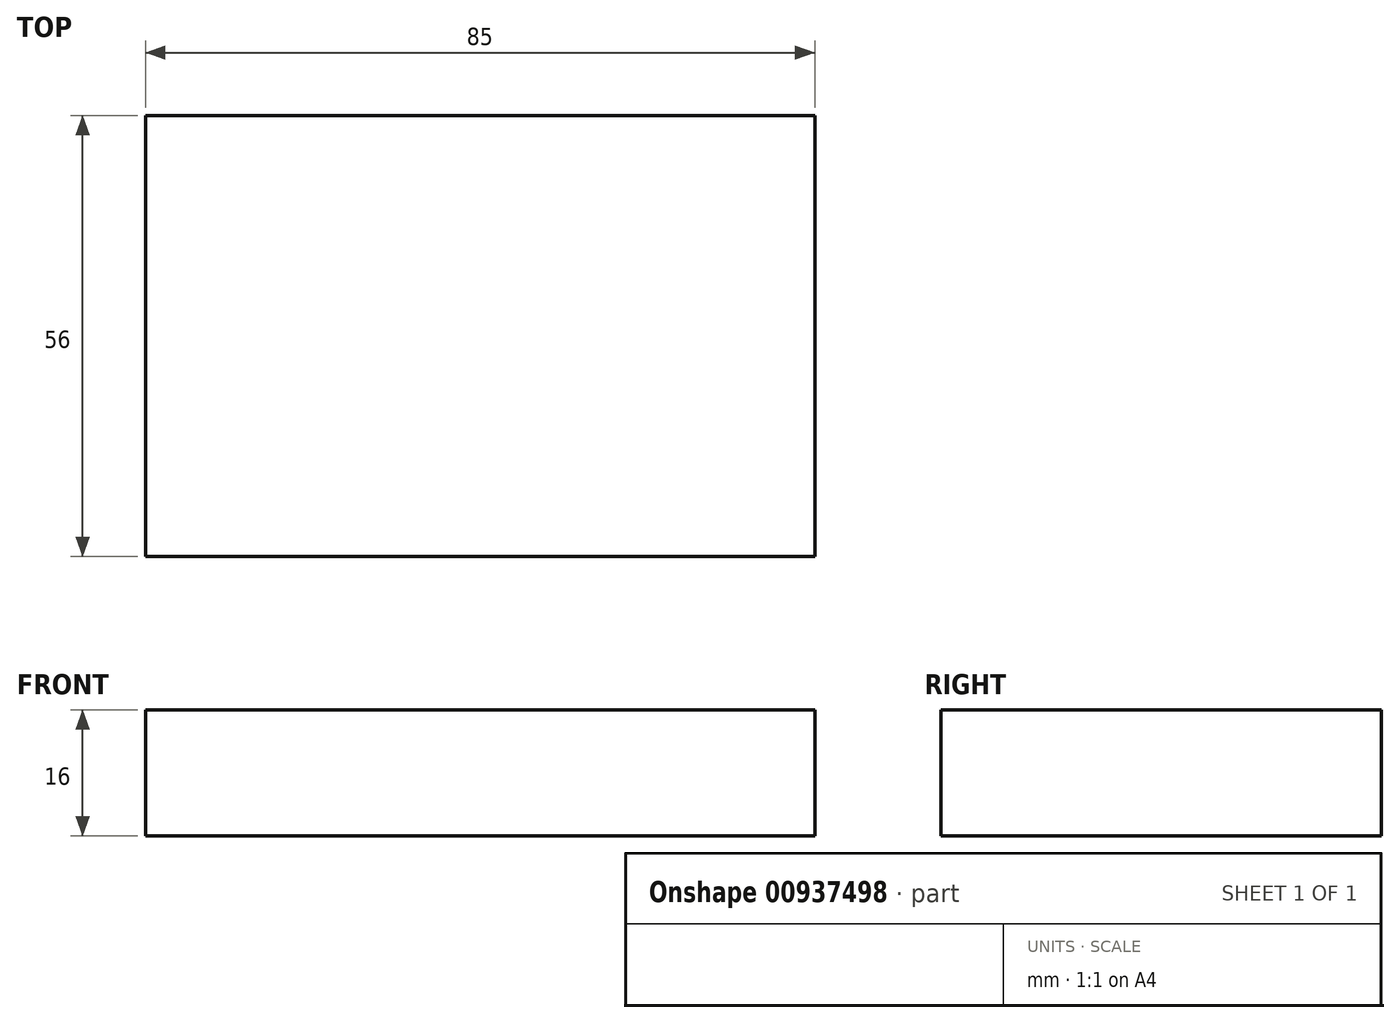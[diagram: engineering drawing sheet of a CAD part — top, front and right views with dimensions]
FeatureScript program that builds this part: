
annotation { "Feature Type Name" : "Feature", "Feature Type Description" : "" }
export const myFeature = defineFeature(function(context is Context, id is Id, definition is map)
    precondition{}
    {
        {
            var Q0;
            Q0=qCreatedBy(makeId("Top.planeOp"),FACE);
            var sketch = newSketch(context, id + "F0", { "sketchPlane" : qUnion([Q0])});
            skLineSegment(sketch, "E0.bottom", {"start": v(42.5, -28) * mm, "end": v(-42.5, -28) * mm});
            skLineSegment(sketch, "E0.top", {"start": v(42.5, 28) * mm, "end": v(-42.5, 28) * mm});
            skLineSegment(sketch, "E0.left", {"start": v(42.5, -28) * mm, "end": v(42.5, 28) * mm});
            skLineSegment(sketch, "E0.right", {"start": v(-42.5, -28) * mm, "end": v(-42.5, 28) * mm});
            skPoint(sketch, "E0.middle", {"position": v(0, 0) * mm});
            skSolve(sketch);
        }
        {
            var Q0;
            Q0=makeQuery(id+"F0.imprint","IMPRINT",FACE,{"disambiguationData":[TD([[makeQuery(id+"F0.imprint","IMPRINT",EDGE,{"derivedFrom":sQuery(id+"F0.wireOp",EDGE,"E0.bottom")}),-1.0]])]});
            extrude(context, id + "F1", {"entities" : qUnion([Q0]), "depth" : 16 * mm, "offsetDistance" : 25.4 * mm});
        }
    });
